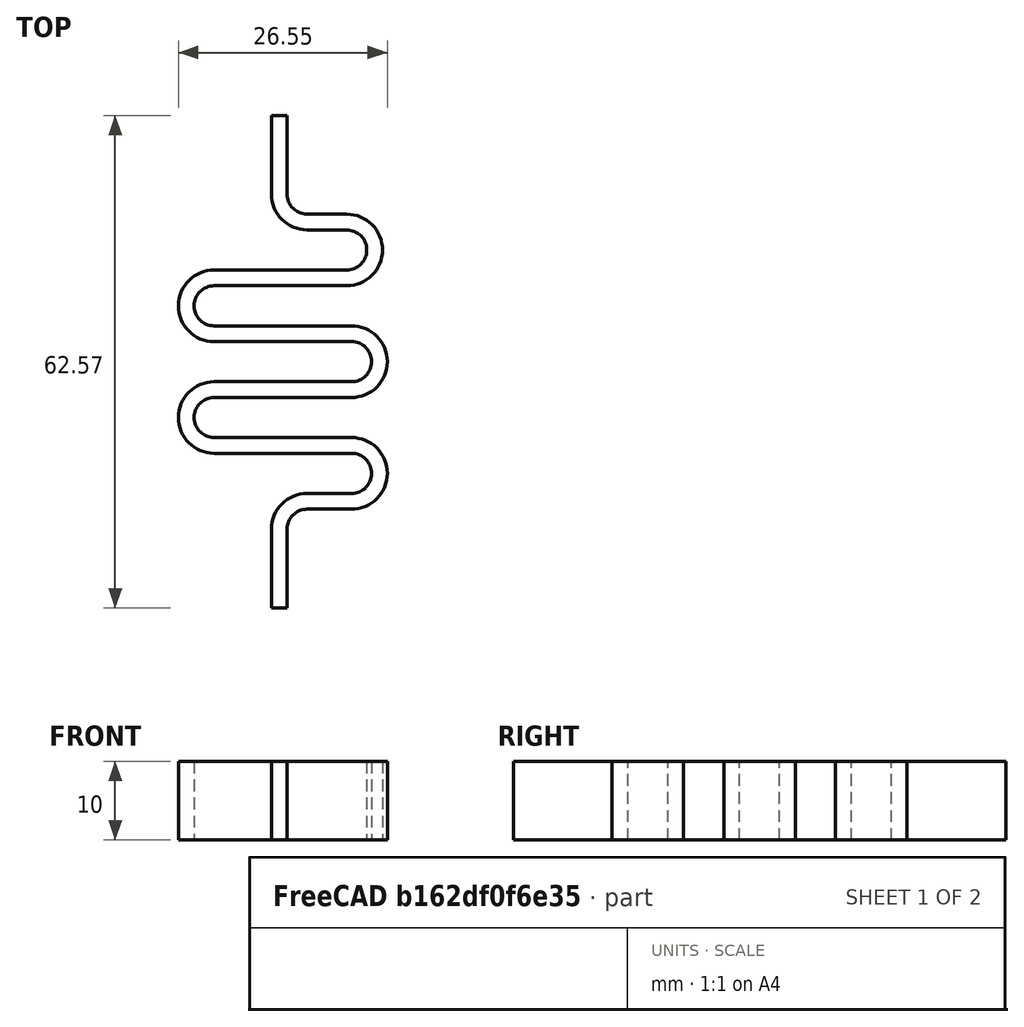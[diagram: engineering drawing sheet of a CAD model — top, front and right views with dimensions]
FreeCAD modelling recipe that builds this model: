
FCSTD DOCUMENT  (FreeCAD 0.19R23756 (Git))
Label: Feder2
License: All rights reserved
LicenseURL: http://en.wikipedia.org/wiki/All_rights_reserved
objects: Sketcher::SketchObject×1, PartDesign::Pad×1, PartDesign::Body×1, Fem::FemSolverObjectPython×1, App::MaterialObjectPython×1, Fem::ConstraintFixed×1, Fem::ConstraintDisplacement×1, Fem::FemMeshShapeNetgenObject×1, Fem::FemAnalysis×1
note: 4 computed .brp shape members not serialized (recipe doc carries the construction recipe); baked Part::Feature solids carry a one-line shape summary decoded from their .brp

FEATURE [Sketcher::SketchObject] Sketch
  FullyConstrained = false
  MapMode = 5
  Support = -> [XY_Plane]
  sketch-geometry (32):
    g0: ArcOfCircle CenterX=-8.26826 CenterY=18.0865 CenterZ=0 NormalX=0 NormalY=0 NormalZ=1 AngleXU=0 Radius=4.54751 StartAngle=1.5708 EndAngle=4.71239
    g1: ArcOfCircle CenterX=9.18269 CenterY=10.9915 CenterZ=0 NormalX=0 NormalY=0 NormalZ=1 AngleXU=0 Radius=4.54751 StartAngle=4.71239 EndAngle=7.85398
    g2: ArcOfCircle CenterX=-8.26826 CenterY=18.0865 CenterZ=0 NormalX=0 NormalY=0 NormalZ=1 AngleXU=0 Radius=2.54751 StartAngle=1.5708 EndAngle=4.71239
    g3: ArcOfCircle CenterX=9.18269 CenterY=10.9915 CenterZ=0 NormalX=0 NormalY=0 NormalZ=1 AngleXU=0 Radius=2.54751 StartAngle=4.71239 EndAngle=7.85398
    g4: LineSegment StartX=-8.26826 StartY=15.539 StartZ=0 EndX=9.18269 EndY=15.539 EndZ=0
    g5: LineSegment StartX=9.18269 StartY=13.539 StartZ=0 EndX=-8.26826 EndY=13.539 EndZ=0
    g6: LineSegment StartX=-8.26826 StartY=20.634 StartZ=0 EndX=9.18269 EndY=20.634 EndZ=0
    g7: LineSegment StartX=-8.26826 StartY=22.634 StartZ=0 EndX=9.18269 EndY=22.634 EndZ=0
    g8: ArcOfCircle CenterX=-8.26826 CenterY=32.2765 CenterZ=0 NormalX=0 NormalY=0 NormalZ=1 AngleXU=0 Radius=4.54751 StartAngle=1.5708 EndAngle=4.71239
    g9: ArcOfCircle CenterX=9.18269 CenterY=25.1815 CenterZ=0 NormalX=0 NormalY=0 NormalZ=1 AngleXU=0 Radius=4.54751 StartAngle=4.71239 EndAngle=7.85398
    g10: ArcOfCircle CenterX=-8.26826 CenterY=32.2765 CenterZ=0 NormalX=0 NormalY=0 NormalZ=1 AngleXU=0 Radius=2.54751 StartAngle=1.5708 EndAngle=4.71239
    g11: ArcOfCircle CenterX=9.18269 CenterY=25.1815 CenterZ=0 NormalX=0 NormalY=0 NormalZ=1 AngleXU=0 Radius=2.54751 StartAngle=4.71239 EndAngle=7.85398
    g12: LineSegment StartX=-8.26826 StartY=29.729 StartZ=0 EndX=9.18269 EndY=29.729 EndZ=0
    g13: LineSegment StartX=9.18269 StartY=27.729 StartZ=0 EndX=-8.26826 EndY=27.729 EndZ=0
    g14: LineSegment StartX=-8.26826 StartY=34.824 StartZ=0 EndX=8.56841 EndY=34.824 EndZ=0
    g15: LineSegment StartX=-8.26826 StartY=36.824 StartZ=0 EndX=8.56841 EndY=36.824 EndZ=0
    g16: ArcOfCircle CenterX=8.56841 CenterY=39.3715 CenterZ=0 NormalX=0 NormalY=0 NormalZ=1 AngleXU=0 Radius=2.54751 StartAngle=4.71239 EndAngle=7.85398
    g17: ArcOfCircle CenterX=8.56841 CenterY=39.3715 CenterZ=0 NormalX=0 NormalY=0 NormalZ=1 AngleXU=0 Radius=4.54751 StartAngle=4.71239 EndAngle=7.85398
    g18: LineSegment StartX=8.56841 StartY=41.919 StartZ=0 EndX=3.54751 EndY=41.919 EndZ=0
    g19: LineSegment StartX=8.56841 StartY=43.919 StartZ=0 EndX=3.54751 EndY=43.919 EndZ=0
    g20: ArcOfCircle CenterX=3.54751 CenterY=46.4665 CenterZ=0 NormalX=0 NormalY=0 NormalZ=1 AngleXU=0 Radius=4.54751 StartAngle=3.14159 EndAngle=4.71239
    g21: ArcOfCircle CenterX=3.54751 CenterY=46.4665 CenterZ=0 NormalX=0 NormalY=0 NormalZ=1 AngleXU=0 Radius=2.54751 StartAngle=3.14159 EndAngle=4.71239
    g22: LineSegment StartX=1 StartY=-6.10356 StartZ=0 EndX=-1 EndY=-6.10356 EndZ=0
    g23: LineSegment StartX=-1 StartY=46.4665 StartZ=0 EndX=-1 EndY=56.4665 EndZ=0
    g24: LineSegment StartX=-1 StartY=56.4665 StartZ=0 EndX=1 EndY=56.4665 EndZ=0
    g25: LineSegment StartX=1 StartY=56.4665 StartZ=0 EndX=1 EndY=46.4665 EndZ=0
    g26: LineSegment StartX=3.54751 StartY=6.44394 StartZ=0 EndX=9.18269 EndY=6.44394 EndZ=0
    g27: LineSegment StartX=9.18269 StartY=8.44394 StartZ=0 EndX=3.54751 EndY=8.44394 EndZ=0
    g28: ArcOfCircle CenterX=3.54751 CenterY=3.89644 CenterZ=0 NormalX=0 NormalY=0 NormalZ=1 AngleXU=0 Radius=4.54751 StartAngle=1.5708 EndAngle=3.14159
    g29: ArcOfCircle CenterX=3.54751 CenterY=3.89644 CenterZ=0 NormalX=0 NormalY=0 NormalZ=1 AngleXU=0 Radius=2.54751 StartAngle=1.5708 EndAngle=3.14159
    g30: LineSegment StartX=-1 StartY=-6.10356 StartZ=0 EndX=-1 EndY=3.89644 EndZ=0
    g31: LineSegment StartX=1 StartY=3.89644 StartZ=0 EndX=1 EndY=-6.10356 EndZ=0
  constraints (69):
    c: Tangent(g8,g15) = 1.5708
    c: Tangent(g10,g14) = 1.5708
    c: Tangent(g10,g12) = -1.5708
    c: Tangent(g8,g13) = 1.5708
    c: Tangent(g9,g12) = 1.5708
    c: Tangent(g11,g13) = -1.5708
    c: Tangent(g7,g11) = -1.5708
    c: Tangent(g6,g9) = -1.5708
    c: Tangent(g0,g7) = 1.5708
    c: Tangent(g2,g6) = 1.5708
    c: Tangent(g2,g4) = -1.5708
    c: Tangent(g0,g5) = 1.5708
    c: Tangent(g1,g4) = 1.5708
    c: Tangent(g3,g5) = -1.5708
    c: Coincident(g0,g2)
    c: Coincident(g8,g10)
    c: Coincident(g9,g11)
    c: Coincident(g1,g3)
    c: Vertical(g0,g0)
    c: Vertical(g0,g0)
    c: Vertical(g0,g2)
    c: Vertical(g2,g2)
    c: Vertical(g7,g8)
    c: Vertical(g8,g8)
    c: Vertical(g8,g8)
    c: Vertical(g8,g10)
    c: Vertical(g10,g10)
    c: Vertical(g1,g1)
    c: Vertical(g1,g3)
    c: Equal(g3,g2)
    c: Equal(g2,g11)
    c: Equal(g11,g10)
    c: Coincident(g17,g16)
    c: Vertical(g17,g17)
    c: Tangent(g15,g16) = -1.5708
    c: Tangent(g14,g17) = -1.5708
    c: Horizontal(g18)
    c: Coincident(g21,g20)
    c: Tangent(g21,g19) = 1.5708
    c: Tangent(g19,g17) = -1.5708
    c: Horizontal(g21,g20)
    c: Tangent(g20,g18) = 1.5708
    c: Tangent(g18,g16) = -1.5708
    c: Equal(g11,g16)
    c: Symmetric(g20,g21,g-2)
    c: DistanceX(g22,g22) = 2
    c: Tangent(g20,g23) = 1.5708
    c: Coincident(g23,g24)
    c: Horizontal(g24)
    c: Coincident(g24,g25)
    c: Coincident(g25,g21)
    c: Vertical(g25)
    c: DistanceY(g20,g23) = 10
    c: Equal(g16,g21)
    c: Coincident(g29,g28)
    c: Tangent(g29,g26) = 1.5708
    c: Tangent(g28,g27) = -1.5708
    c: Coincident(g30,g22)
    c: Vertical(g30)
    c: Coincident(g31,g22)
    c: Vertical(g31)
    c: Tangent(g3,g27) = 1.5708
    c: Tangent(g1,g26) = -1.5708
    c: Tangent(g31,g29) = -1.5708
    c: Tangent(g30,g28) = 1.5708
    c: Equal(g29,g3)
    c: Symmetric(g22,g22,g-2)
    c: DistanceY(g22,g29) = 10
    c: Vertical(g1,g9)
FEATURE [PartDesign::Pad] Pad
  Direction = (1,1,1)
  Length = 10
  Length2 = 100
  Profile = -> Sketch
  Type = 0
FEATURE [PartDesign::Body] Body
  Group = -> [Sketch,Pad]
  Origin = -> Origin
  Tip = -> Pad
FEATURE [Fem::FemSolverObjectPython] SolverCcxTools  # FEM object (typed FeaturePython)
  AnalysisType = 0
  BeamShellResultOutput3D = false
  EigenmodeHighLimit = 1000000
  EigenmodeLowLimit = 0
  EigenmodesCount = 10
  GeometricalNonlinearity = 0
  IterationsControlParameterCutb = 0.25,0.5,0.75,0.85,,,1.5,
  IterationsControlParameterIter = 4,8,9,200,10,400,,200,,
  IterationsControlParameterTimeUse = false
  IterationsThermoMechMaximum = 2000
  IterationsUserDefinedIncrementations = false
  IterationsUserDefinedTimeStepLength = false
  MaterialNonlinearity = 0
  MatrixSolverType = 0
  SplitInputWriter = false
  ThermoMechSteadyState = true
  TimeEnd = 1
  TimeInitialStep = 0.01
FEATURE [App::MaterialObjectPython] MaterialSolid  # material (typed FeaturePython)
  Category = 0
  Material = AuthorAndLicense=PLA-Generic,CardName=PLA-Generic,Density=1240 kg/m^3,+12 more (map truncated)
FEATURE [Fem::ConstraintFixed] ConstraintFixed
  NormalDirection = (0,1,0)
  Normals = (9) [(0,1,0),(0,1,0),(0,1,0),(0,1,0),(0,1,0),(0,1,0),(0,1,0),(0,1,0),(0,1,0)]
  Points = (9) [(-1,56.4665,10),(5.55112e-16,56.4665,10),(1,56.4665,10),(-1,56.4665,5),(5.55112e-16,56.4665,5),(1,56.4665,5),(-1,56.4665,0),(5.55112e-16,56.4665,0),(1,56.4665,0)]
  References = -> [Pad]
FEATURE [Fem::ConstraintDisplacement] ConstraintDisplacement
  NormalDirection = (-4e-16,-1,0)
  Normals = (9) [(-4.4e-16,-1,0),(-4.4e-16,-1,0),(-4.4e-16,-1,0),(-4.4e-16,-1,0),(-4.4e-16,-1,0),(-4.4e-16,-1,0),(-4.4e-16,-1,0),(-4.4e-16,-1,0),(-4.4e-16,-1,0)]
  Points = (9) [(1,-6.10356,10),(0,-6.10356,10),(-1,-6.10356,10),(1,-6.10356,5),(0,-6.10356,5),(-1,-6.10356,5),(1,-6.10356,0),(0,-6.10356,0),(-1,-6.10356,0)]
  References = -> [Pad]
  rotxFix = false
  rotxFree = true
  rotyFix = false
  rotyFree = true
  rotzFix = false
  rotzFree = true
  xDisplacement = 0
  xFix = false
  xFree = true
  xRotation = 0
  yDisplacement = -20
  yFix = false
  yFree = false
  yRotation = 0
  zDisplacement = 0
  zFix = false
  zFree = true
  zRotation = 0
FEATURE [Fem::FemMeshShapeNetgenObject] FEMMeshNetgen
  Fineness = 2
  GrowthRate = 0.3
  MaxSize = 1000
  NbSegsPerEdge = 1
  NbSegsPerRadius = 2
  Optimize = true
  SecondOrder = true
  Shape = -> Pad
FEATURE [Fem::FemAnalysis] Analysis
  Group = -> [SolverCcxTools,MaterialSolid,ConstraintFixed,ConstraintDisplacement,FEMMeshNetgen]
